# Revit family: RVi-IPC44 (3.0-12мм)
name_source: partatom
category: Устройства связи
revit_build: Autodesk Revit 2016 (Build: 20161004_0715(x64)
units: mm (PartAtom-declared; Revit-internal decimal feet)

## family parameters
Всегда вертикально = Да
На основе рабочей плоскости = Да
Общий = Нет
При загрузке вырезать с полостями = Нет
Размер круглого соединителя = Использовать диаметр
Сохранять ориентацию аннотаций = Нет
Тип детали = Нормальный
Точка расчета площади = Нет

## types (1)
- Стандартная
    2D.Телекамера в герметичном термокожухе = Нет
    2D.Телекамера с поворотным устройством = Нет
    Bullet.корпус = Корпус 44 : Тип
    Bullet.крепление = Корпус 44.крепление : Тип
    Kr_max = 360.00°
    Kr_min = -360.00°
    RVi.Аудио.Вход = Нет
    RVi.Аудио.Выход = Нет
    RVi.Аудио.Динамик = Нет
    RVi.Аудио.Микрофон = Нет
    RVi.ИК подсветка.Дальность = 30000 мм
    RVi.Карта памяти = Нет
    RVi.Питание 12В = Да
    RVi.Питание 24В = Нет
    RVi.Питание POE = Да
    RVi.Разрешение = 2688×1520
    RVi.Тип корпуса = Уличные-Bullet
    RVi.Тип продукта = Камеры уличные
    RVi.Тревога = Нет
    RVi.Функция аналитики = Нет
    Rn_max = 90.00°
    Rn_min = -90.00°
    Ro_max = 90.00°
    Ro_min = -90.00°
    URL = http://rvi-cctv.ru
    Ug_max = 77.00°
    Ug_min = 23.00°
    Uv_max = 50.00°
    Uv_min = 13.00°
    Вращение всей камеры = 0.00°
    Группа модели = Камера в сборе
    Длина неподвижной части корпуса = 72 мм
    Длина подвижной части = 172 мм
    Изготовитель = RVi
    К идентификации = 250
    К обнаружения = 20
    К распознавания номера = 240
    К распознования = 100
    Крепление = Без крепления : Пусто
    Купол.корпус = Без корпуса : Пусто
    Купол.обектив = Без корпуса : Пусто
    Купольная камера = Нет
    Материал корпуса камеры = Камера.корпус
    Материал крепления = Камера.крепление
    Материал объектива камеры = Камера.объектив
    Наименование и техническая характеристика = Уличная IP-камера; 1/3'' КМОП-матрица, 4 Мегапикселя; Разрешение и скорость трансляции: 2688х1512 @ 15 к/с, 2304х1296 @ 20 к/с, 1920х1080 @ 25 к/с,;Нижний порог чувствительности: 0.01 лк @ F1.6 цвет / 0 лк (ИК вкл.) ; Фариофокальный объектив: 3.0-12 мм  ; ИК-подсветка: до 30 метров; Запись на MicroSD карту до 128 ГБ;  Класс защиты: IP66; Диапазон рабочих температур: -40…+50°С; Питание: PoE 802.3af / DC 12 В, до 7.5 Вт.
    Обектив коррекция наклона = 90.00°
    Отметка по умолчанию = 1219 мм
    Поворот направления взгляда = 180.00°
    Смещение объектива = 0 мм
    Стрела длина = 0 мм
    Стрела коррекция = 0.00°
    Стрела угол подъема = 0.00°
    УГО смещение = 0 мм
    да = Да
    нет = Нет

## geometry (parser evidence)
native form markers: Blend x2
no freeform markers — native parametric forms only
